# Revit family: DownlightConcreto_DLRC-SBP9W_DLRC-SBP18W_PowerLume
name_source: partatom
category: Luminárias
units: mm (PartAtom-declared; Revit-internal decimal feet)

## family parameters
Compartilhado = Sim
Corte com vazios quando carregada = Sim
Cota do conector redondo = Utilizar diâmetro
Fonte luminosa = Não
Hospedeiro = Face
Manter orientação da anotação = Não
Número OmniClass = 23.80.70.14.17
Ponto de cálculo do ambiente = Não
Tipo de parte = Normal
Título OmniClass = Exterior Spotlights

## types (2) — shared parameters
Carga Aparente Luminária = 0 VA
Catálogo de produtos = https://www.powerlume.com.br
Comentários de voltagem = 110 ou 220Vac 50/60Hz com driver incorporado
Contato do fabricante = (54) 3066-6488
Data da atualização = 27/02/2025
Descrição = Downlight de sobrepor LED em concreto
Elevação-padrão = 1219 mm
Fabricante = Power Lume
Fator de Potência Luminária = 1
Frame = Concreto, leve
IP = 65
IRC = 85
IfcExportAs = IfcLightFixtureType
Localização = Caxias do Sul - RS / Brasil
Lâmpada = Placa LED
Peso = 0
Refletor = Metal - Alumínio Anodizado
Temperatura de cor = 3000K
URL = https://www.powerlume.com.br
URL do produto = https://www.powerlume.com.br
Versão = 1
Vida útil = 60000h
Voltagem Luminária = 0 V
Ângulo de abertura = 80°

## per-type parameters (varying)
| type | Altura | Diâmetro | Fluxo luminoso | Modelo de luminária | Potência | Tipo de imagem |
| DLRC-SBP9W | 120 mm  [stored 0.393701 ft] | 102 mm | 1170 lm | DownlightConcreto_DLRC-SBP9W_Base_PowerLume : DLRC-SBP9W | 9W | FOTO DLRC-SBP9W.png |
| DLRC-SBP18W | 150 mm | 175 mm  [stored 0.574147 ft] | 2340 lm | DownlightConcreto_DLRC-SBP18W_Base_PowerLume : DLRC-SBP18W | 18W | FOTO DLRC-SBP18W.png |

note: column(s) folded — value = type name in every type: Modelo

note: [stored X ft] marks values corroborated as IEEE doubles in the binary element streams (Revit-internal decimal feet)
